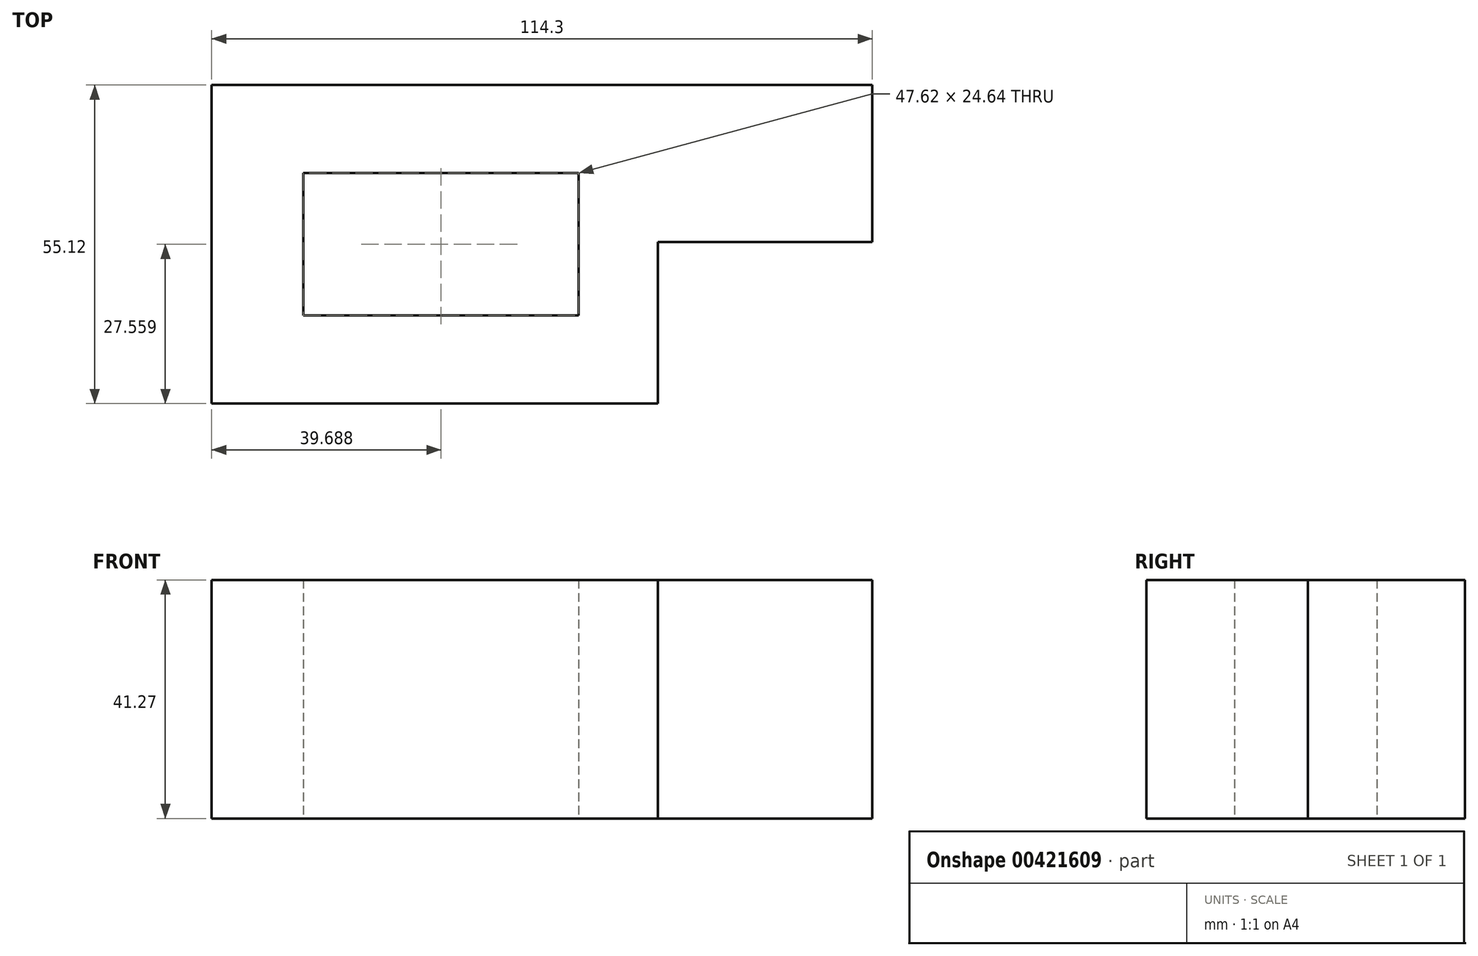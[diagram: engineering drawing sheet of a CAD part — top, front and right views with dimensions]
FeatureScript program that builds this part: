
annotation { "Feature Type Name" : "Feature", "Feature Type Description" : "" }
export const myFeature = defineFeature(function(context is Context, id is Id, definition is map)
    precondition{}
    {
        {
            var Q0;
            Q0=qCreatedBy(makeId("Top.planeOp"),FACE);
            var sketch = newSketch(context, id + "F0", { "sketchPlane" : qUnion([Q0])});
            skLineSegment(sketch, "E0.bottom", {"start": v(0, 0) * mm, "end": v(77.22, 0) * mm});
            skLineSegment(sketch, "E0.top", {"start": v(0, 55.12) * mm, "end": v(114.3, 55.12) * mm});
            skLineSegment(sketch, "E0.left", {"start": v(0, 0) * mm, "end": v(0, 55.12) * mm});
            skLineSegment(sketch, "E0.right", {"start": v(114.3, 27.94) * mm, "end": v(114.3, 55.12) * mm});
            skLineSegment(sketch, "E1", {"start": v(114.3, 27.94) * mm, "end": v(77.22, 27.94) * mm});
            skLineSegment(sketch, "E2", {"start": v(77.22, 27.94) * mm, "end": v(77.22, 0) * mm});
            skLineSegment(sketch, "E3.bottom", {"start": v(15.88, 15.24) * mm, "end": v(63.5, 15.24) * mm});
            skLineSegment(sketch, "E3.top", {"start": v(15.88, 39.88) * mm, "end": v(63.5, 39.88) * mm});
            skLineSegment(sketch, "E3.left", {"start": v(15.88, 15.24) * mm, "end": v(15.88, 39.88) * mm});
            skLineSegment(sketch, "E3.right", {"start": v(63.5, 15.24) * mm, "end": v(63.5, 39.88) * mm});
            skSolve(sketch);
        }
        {
            var Q0;
            Q0 = qSketchRegion(id + "F0", true);
            extrude(context, id + "F1", {"entities" : qUnion([Q0]), "depth" : 41.27 * mm});
        }
    });
